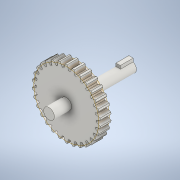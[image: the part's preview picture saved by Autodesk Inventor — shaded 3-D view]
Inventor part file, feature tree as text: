
AUTODESK INVENTOR PART (.ipt)
format: ipt  version: 2021 (Build 250183000, 183)  size: 294,912 bytes
history: native  units: mm (DEFAULTED — no unit token found)
features: sketch x5, extrude x4, plane x3, other x3
ambient origin geometry x8: Origin, YZ Plane, XZ Plane, XY Plane, X Axis, Y Axis, Z Axis, Center Point
bodies: Solid1 (feature_tree)
feature tree (15):
  extrude  "Extrusion1"  Depth=5.0mm TaperAngle=0.0deg
  plane  "Work Plane2"
  plane  "Work Plane8"
  plane  "Work Plane9"
  other  "Spur Gear"
  extrude  "Extrusion4"  Depth=10.0mm TaperAngle=0.0deg
  extrude  "Extrusion5"  Depth=1.047198mm TaperAngle=0.0deg
  extrude  "Extrusion6"  TaperAngle=0.0deg  [1 undecoded]
  sketch  "Sketch1"  dims[d0=31.6mm d1=5.0mm d2=0.0mm]
  sketch  "Sketch2"  dims[d3=30.0mm d4=10.0mm d5=0.0mm]
  other  "Srf1"
  sketch  "Sketch6"  dims[d16=22.5mm d17=0.0mm d34=1.047198mm]
  sketch  "Sketch7"  dims[d39=0.0mm d41=0.0mm]
  sketch  "Sketch8"  dims[d43=22.5mm d46=22.5mm d47=0.0mm d48=0.0mm d68=5.0mm d73=25.0mm d74=0.0mm d75=2.0mm d76=1.5mm d77=6.0mm d78=0.0mm d79=5.0mm d80=8.0mm d81=0.0mm d59=0.5mm d60=0.872665mm d61=0.5mm d62=0.872665mm]
  other  "Pitch Diameter"
note: 1 required parameter value undecoded (feature->parameter linkage not recoverable at this tier; creation-order binding heuristic only, values carry confidence <= 0.55)
